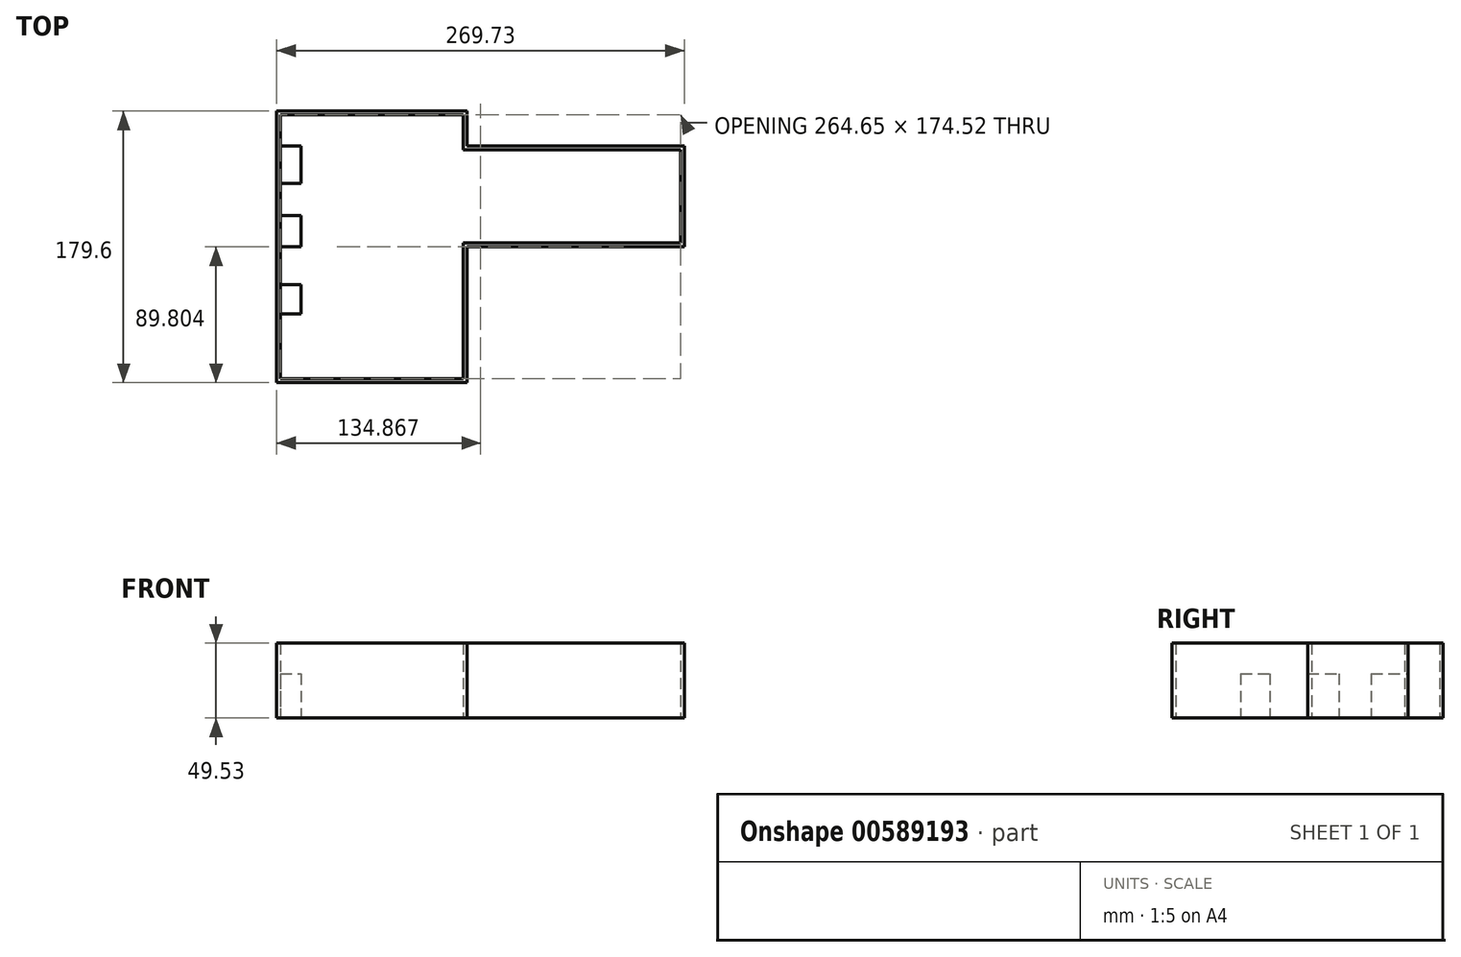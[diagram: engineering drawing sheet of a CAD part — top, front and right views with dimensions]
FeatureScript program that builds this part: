
annotation { "Feature Type Name" : "Feature", "Feature Type Description" : "" }
export const myFeature = defineFeature(function(context is Context, id is Id, definition is map)
    precondition{}
    {
        {
            var Q0;
            Q0=qCreatedBy(makeId("Top.planeOp"),FACE);
            var sketch = newSketch(context, id + "F0", { "sketchPlane" : qUnion([Q0])});
            skLineSegment(sketch, "E0.bottom", {"start": v(-16.27, 9.44) * mm, "end": v(109.73, 9.44) * mm});
            skLineSegment(sketch, "E0.top", {"start": v(-16.27, 189.04) * mm, "end": v(109.73, 189.04) * mm});
            skLineSegment(sketch, "E0.left", {"start": v(-16.27, 9.44) * mm, "end": v(-16.27, 189.04) * mm});
            skLineSegment(sketch, "E0.right", {"start": v(109.73, 9.44) * mm, "end": v(109.73, 189.04) * mm});
            skLineSegment(sketch, "E1.bottom", {"start": v(253.46, 165.87) * mm, "end": v(109.73, 165.87) * mm});
            skLineSegment(sketch, "E1.top", {"start": v(253.46, 99.24) * mm, "end": v(109.73, 99.24) * mm});
            skLineSegment(sketch, "E1.left", {"start": v(253.46, 165.87) * mm, "end": v(253.46, 99.24) * mm});
            skLineSegment(sketch, "E1.right", {"start": v(109.73, 165.87) * mm, "end": v(109.73, 99.24) * mm});
            skSolve(sketch);
        }
        {
            var Q0;
            {var subQ1=sQuery(id+"F0.wireOp",EDGE,"E0.bottom");Q0=makeQuery(id+"F0.imprint","IMPRINT",FACE,{"disambiguationData":[TD([[makeQuery(id+"F0.imprint","IMPRINT",EDGE,{"derivedFrom":subQ1}),1.0]])]});}
            var Q1;
            Q1=makeQuery(id+"F0.imprint","IMPRINT",FACE,{"disambiguationData":[TD([[makeQuery(id+"F0.imprint","IMPRINT",EDGE,{"derivedFrom":sQuery(id+"F0.wireOp",EDGE,"E1.bottom")}),1.0]])]});
            extrude(context, id + "F1", {"entities" : qUnion([Q0, Q1]), "depth" : 49.53 * mm, "offsetDistance" : 25.4 * mm});
        }
        {
            var Q0;
            Q0=makeQuery(id+"F1.opExtrude","CAP_FACE",FACE,{"disambiguationData":[OSD([sQuery(id+"F0.wireOp",EDGE,"E0.bottom"),sQuery(id+"F0.wireOp",EDGE,"E0.top"),sQuery(id+"F0.wireOp",EDGE,"E0.left"),sQuery(id+"F0.wireOp",EDGE,"E0.right"),sQuery(id+"F0.wireOp",EDGE,"E1.bottom"),sQuery(id+"F0.wireOp",EDGE,"E1.top"),sQuery(id+"F0.wireOp",EDGE,"E1.left")])],"isStart":false});
            var Q1;
            Q1=makeQuery(id+"F1.opExtrude","CAP_FACE",FACE,{"disambiguationData":[OSD([sQuery(id+"F0.wireOp",EDGE,"E0.bottom"),sQuery(id+"F0.wireOp",EDGE,"E0.top"),sQuery(id+"F0.wireOp",EDGE,"E0.left"),sQuery(id+"F0.wireOp",EDGE,"E0.right"),sQuery(id+"F0.wireOp",EDGE,"E1.bottom"),sQuery(id+"F0.wireOp",EDGE,"E1.top"),sQuery(id+"F0.wireOp",EDGE,"E1.left")])],"isStart":true});
            shell(context, id + "F2", {"entities" : qUnion([Q0, Q1]), "thickness" : 2.54 * mm});
        }
        {
            var Q0;
            Q0=qCreatedBy(makeId("Top.planeOp"),FACE);
            var sketch = newSketch(context, id + "F3", { "sketchPlane" : qUnion([Q0])});
            skLineSegment(sketch, "E2.0", {"start": v(-13.73, 11.98) * mm, "end": v(-13.73, 186.5) * mm, "construction": true});
            skLineSegment(sketch, "E3.0", {"start": v(-13.73, 186.5) * mm, "end": v(107.2, 186.5) * mm, "construction": true});
            skLineSegment(sketch, "E4.bottom", {"start": v(-13.73, 54.88) * mm, "end": v(0, 54.88) * mm});
            skLineSegment(sketch, "E4.top", {"start": v(-13.73, 74.24) * mm, "end": v(0, 74.24) * mm});
            skLineSegment(sketch, "E4.left", {"start": v(-13.73, 54.88) * mm, "end": v(-13.73, 74.24) * mm, "construction": true});
            skLineSegment(sketch, "E4.right", {"start": v(0, 54.88) * mm, "end": v(0, 74.24) * mm});
            skLineSegment(sketch, "E5.bottom", {"start": v(-13.73, 99.24) * mm, "end": v(0, 99.24) * mm});
            skLineSegment(sketch, "E5.top", {"start": v(-13.73, 120.08) * mm, "end": v(0, 120.08) * mm});
            skLineSegment(sketch, "E5.left", {"start": v(-13.73, 99.24) * mm, "end": v(-13.73, 120.08) * mm, "construction": true});
            skLineSegment(sketch, "E5.right", {"start": v(0, 99.24) * mm, "end": v(0, 120.08) * mm});
            skLineSegment(sketch, "E6.bottom", {"start": v(-13.73, 141.32) * mm, "end": v(0, 141.32) * mm});
            skLineSegment(sketch, "E6.top", {"start": v(-13.73, 165.88) * mm, "end": v(0, 165.88) * mm});
            skLineSegment(sketch, "E6.left", {"start": v(-13.73, 141.32) * mm, "end": v(-13.73, 165.88) * mm, "construction": true});
            skLineSegment(sketch, "E6.right", {"start": v(0, 141.32) * mm, "end": v(0, 165.88) * mm});
            skLineSegment(sketch, "E7", {"start": v(-13.73, 54.88) * mm, "end": v(-13.73, 74.24) * mm});
            skLineSegment(sketch, "E8", {"start": v(-13.73, 99.24) * mm, "end": v(-13.73, 120.08) * mm});
            skLineSegment(sketch, "E9", {"start": v(-13.73, 141.32) * mm, "end": v(-13.73, 165.88) * mm});
            skSolve(sketch);
        }
        {
            var Q0;
            Q0 = qSketchRegion(id + "F3", true);
            extrude(context, id + "F4", {"entities" : qUnion([Q0]), "operationType" : NewBodyOperationType.ADD, "depth" : 29.46 * mm, "offsetDistance" : 25.4 * mm});
        }
    });
